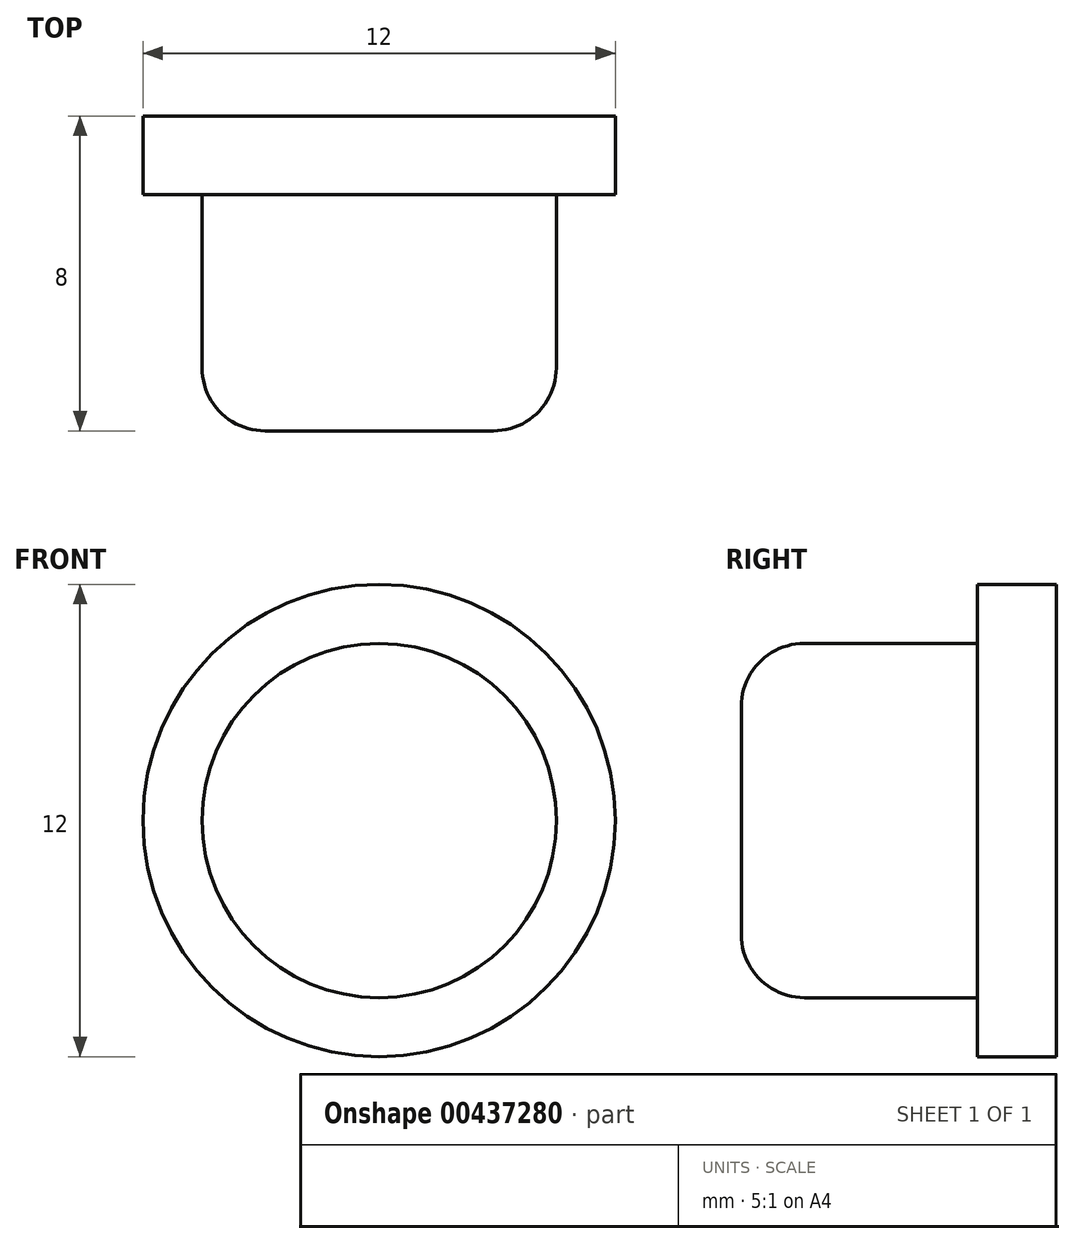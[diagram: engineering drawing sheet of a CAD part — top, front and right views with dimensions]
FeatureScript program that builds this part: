
annotation { "Feature Type Name" : "Feature", "Feature Type Description" : "" }
export const myFeature = defineFeature(function(context is Context, id is Id, definition is map)
    precondition{}
    {
        {
            var Q0;
            Q0=qCreatedBy(makeId("Front.planeOp"),FACE);
            var sketch = newSketch(context, id + "F0", { "sketchPlane" : qUnion([Q0])});
            skCircle(sketch, "E0", {"center": v(0, 0) * mm, "radius": 6 * mm});
            skSolve(sketch);
        }
        {
            var Q0;
            Q0=makeQuery(id+"F0.imprint","IMPRINT",FACE,{"disambiguationData":[TD([[makeQuery(id+"F0.imprint","IMPRINT",EDGE,{"derivedFrom":sQuery(id+"F0.wireOp",EDGE,"E0")}),1.0]])]});
            extrude(context, id + "F1", {"entities" : qUnion([Q0]), "depth" : 2 * mm});
        }
        {
            var Q0;
            Q0=makeQuery(id+"F1.opExtrude","CAP_FACE",FACE,{"disambiguationData":[OSD([sQuery(id+"F0.wireOp",EDGE,"E0")])],"isStart":false});
            var sketch = newSketch(context, id + "F2", { "sketchPlane" : qUnion([Q0])});
            skCircle(sketch, "E1", {"center": v(0, 0) * mm, "radius": 4.5 * mm});
            skSolve(sketch);
        }
        {
            var Q0;
            Q0 = qSketchRegion(id + "F2", true);
            extrude(context, id + "F3", {"entities" : qUnion([Q0]), "operationType" : NewBodyOperationType.ADD, "depth" : 6 * mm});
        }
        {
            var Q0;
            Q0=makeQuery(id+"F3.opExtrude","CAP_EDGE",EDGE,{"disambiguationData":[OSD([sQuery(id+"F2.wireOp",EDGE,"E1")])],"isStart":false});
            fillet(context, id + "F4", {"entities" : qUnion([Q0]), "radius" : 1.6 * mm, "tangentPropagation" : true, "allowEdgeOverflow" : false});
        }
    });
